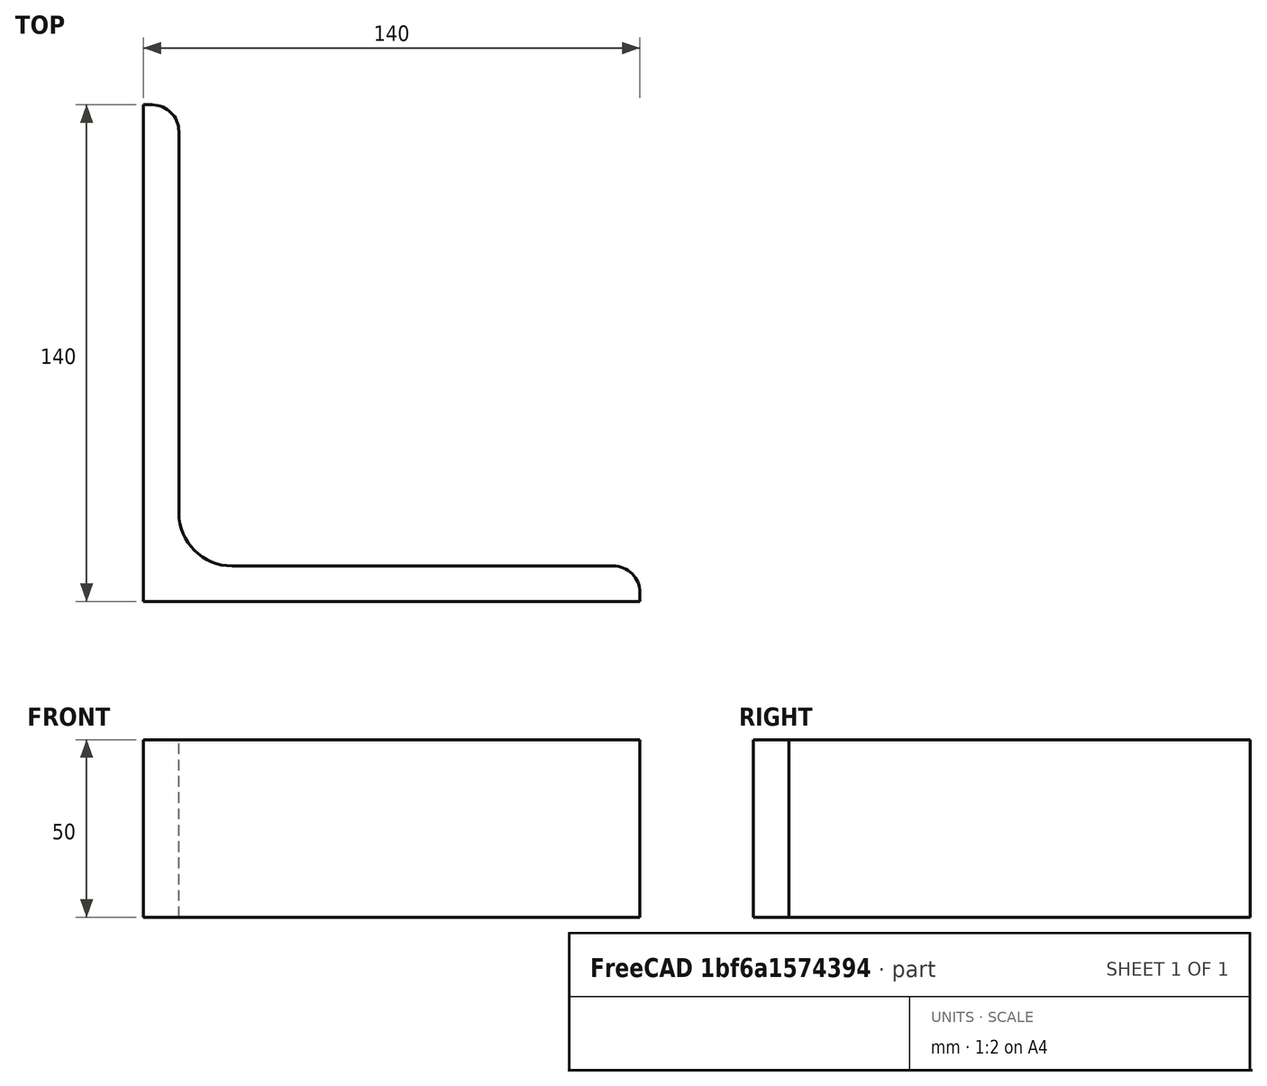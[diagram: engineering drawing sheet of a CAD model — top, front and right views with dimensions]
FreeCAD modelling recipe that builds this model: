
FCSTD DOCUMENT  (FreeCAD 0.15R4671 (Git))
Label: Angle Bar L140x140x10 EN10056 S235JR
License: All rights reserved
LicenseURL: http://en.wikipedia.org/wiki/All_rights_reserved
objects: Sketcher::SketchObject×1, Part::Extrusion×1
note: 2 computed .brp shape members not serialized (recipe doc carries the construction recipe); baked Part::Feature solids carry a one-line shape summary decoded from their .brp

FEATURE [Sketcher::SketchObject] Sketch
  sketch-geometry (9):
    g0: LineSegment StartX=0 StartY=0 StartZ=0 EndX=140 EndY=0 EndZ=0
    g1: LineSegment StartX=140 StartY=0 StartZ=0 EndX=140 EndY=2.5 EndZ=0
    g2: LineSegment StartX=132.5 StartY=10 StartZ=0 EndX=25 EndY=10 EndZ=0
    g3: LineSegment StartX=0 StartY=0 StartZ=0 EndX=0 EndY=140 EndZ=0
    g4: LineSegment StartX=0 StartY=140 StartZ=0 EndX=2.5 EndY=140 EndZ=0
    g5: LineSegment StartX=10 StartY=132.5 StartZ=0 EndX=10 EndY=25 EndZ=0
    g6: ArcOfCircle CenterX=25 CenterY=25 CenterZ=0 NormalX=0 NormalY=0 NormalZ=1 Radius=15 StartAngle=3.14159 EndAngle=4.71239
    g7: ArcOfCircle CenterX=2.5 CenterY=132.5 CenterZ=0 NormalX=0 NormalY=0 NormalZ=1 Radius=7.5 StartAngle=0 EndAngle=1.5708
    g8: ArcOfCircle CenterX=132.5 CenterY=2.5 CenterZ=0 NormalX=0 NormalY=0 NormalZ=1 Radius=7.5 StartAngle=0 EndAngle=1.5708
  constraints (23):
    c: Coincident(g0,g-1)
    c: Horizontal(g0)
    c: Coincident(g1,g0)
    c: Vertical(g1)
    c: Horizontal(g2)
    c: Coincident(g3,g-1)
    c: Vertical(g3)
    c: Coincident(g4,g3)
    c: Horizontal(g4)
    c: Vertical(g5)
    c: Tangent(g5,g6) = -1.5708
    c: Tangent(g2,g6) = 1.5708
    c: Tangent(g4,g7) = 1.5708
    c: Tangent(g5,g7) = 1.5708
    c: Tangent(g2,g8) = -1.5708
    c: Tangent(g1,g8) = -1.5708
    c: DistanceX(g0) = 140
    c: DistanceY(g3) = 140
    c: DistanceY(g0,g2) = 10
    c: DistanceX(g3,g5) = 10
    c: Radius(g6) = 15
    c: Radius(g8) = 7.5
    c: Radius(g7) = 7.5
FEATURE [Part::Extrusion] Extrude  label="Angle Bar L140x140x10 EN10056 S235JR"
  Base = -> Sketch
  Dir = (0,0,50)
  Solid = true
